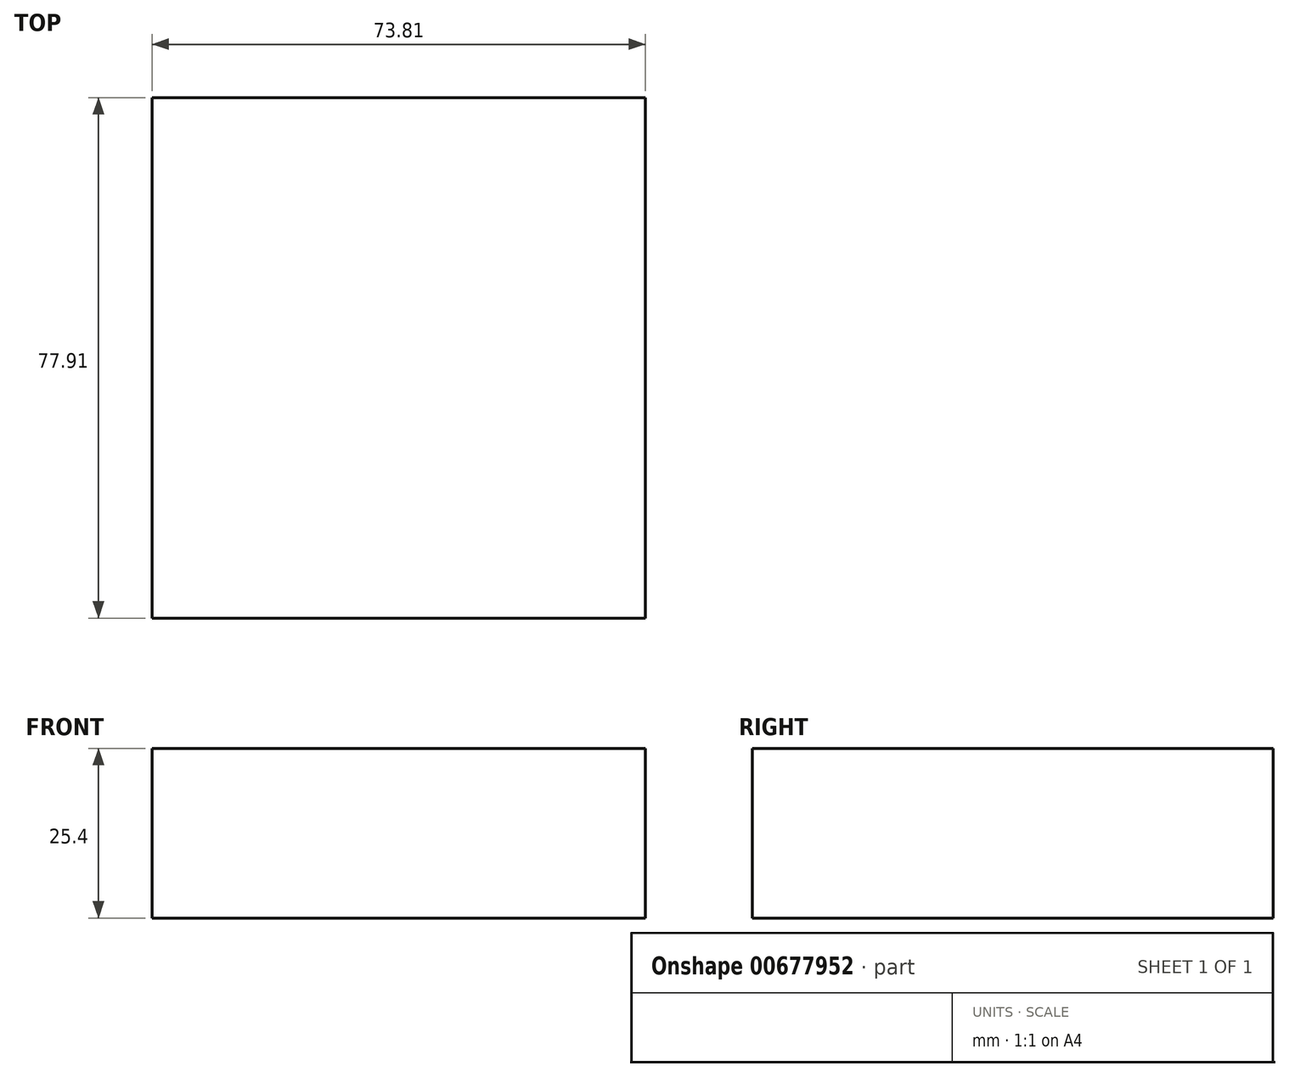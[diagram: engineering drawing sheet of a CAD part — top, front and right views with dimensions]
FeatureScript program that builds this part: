
annotation { "Feature Type Name" : "Feature", "Feature Type Description" : "" }
export const myFeature = defineFeature(function(context is Context, id is Id, definition is map)
    precondition{}
    {
        {
            var Q0;
            Q0=qCreatedBy(makeId("Top.planeOp"),FACE);
            var sketch = newSketch(context, id + "F0", { "sketchPlane" : qUnion([Q0])});
            skLineSegment(sketch, "E0.bottom", {"start": v(-32.23, 36.94) * mm, "end": v(41.58, 36.94) * mm});
            skLineSegment(sketch, "E0.top", {"start": v(-32.23, -40.97) * mm, "end": v(41.58, -40.97) * mm});
            skLineSegment(sketch, "E0.left", {"start": v(-32.23, 36.94) * mm, "end": v(-32.23, -40.97) * mm});
            skLineSegment(sketch, "E0.right", {"start": v(41.58, 36.94) * mm, "end": v(41.58, -40.97) * mm});
            skSolve(sketch);
        }
        {
            var Q0;
            Q0=makeQuery(id+"F0.imprint","IMPRINT",FACE,{"disambiguationData":[TD([[makeQuery(id+"F0.imprint","IMPRINT",EDGE,{"derivedFrom":sQuery(id+"F0.wireOp",EDGE,"E0.bottom")}),-1.0]])]});
            extrude(context, id + "F1", {"entities" : qUnion([Q0]), "depth" : 25.4 * mm, "offsetDistance" : 25.4 * mm});
        }
    });
